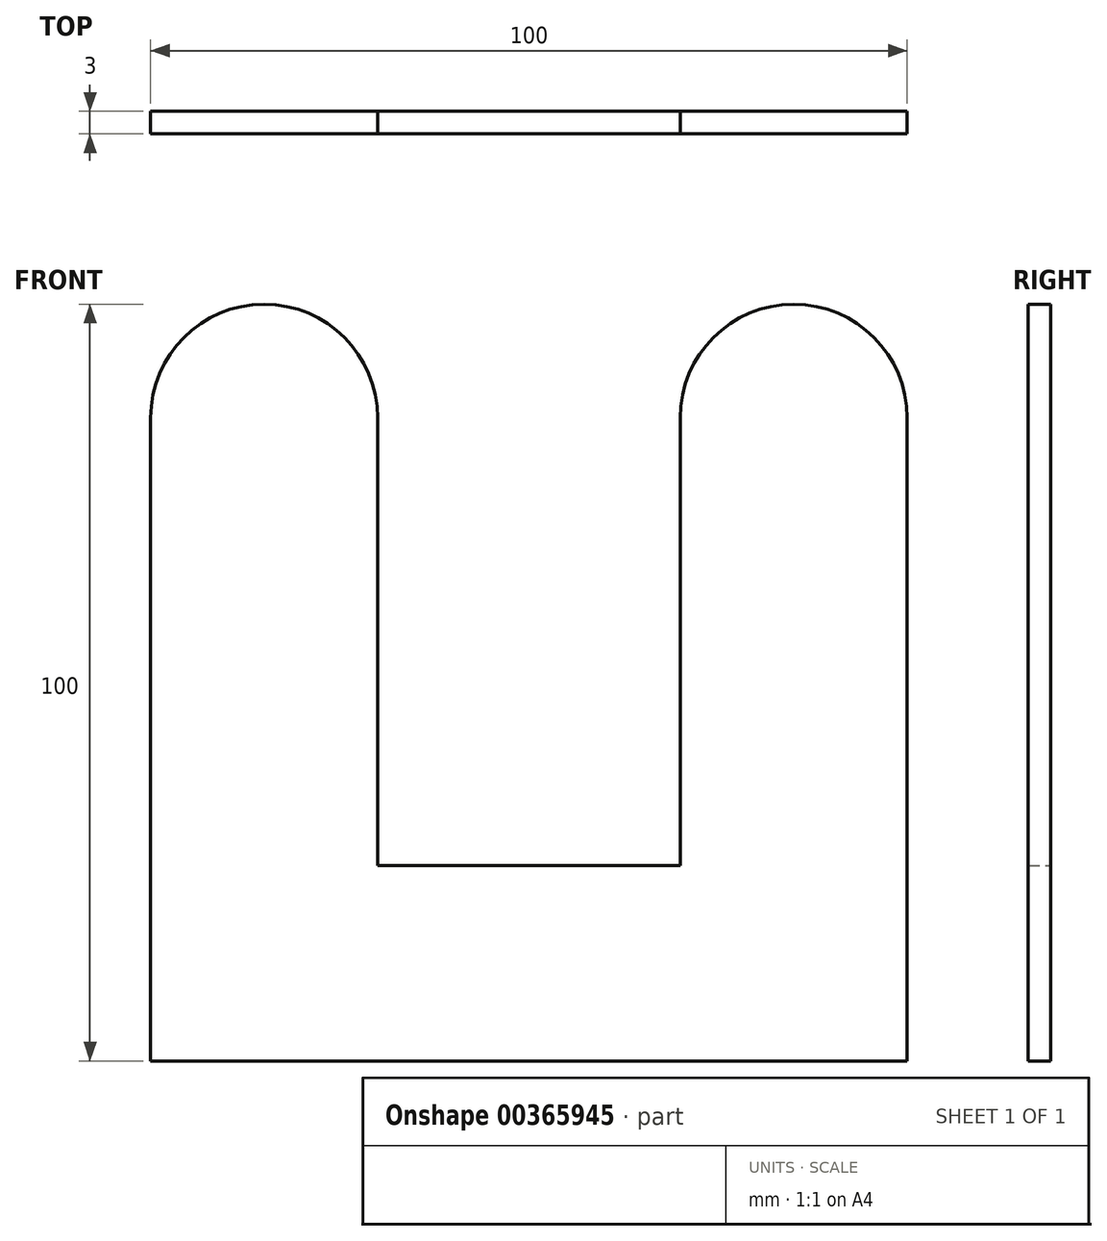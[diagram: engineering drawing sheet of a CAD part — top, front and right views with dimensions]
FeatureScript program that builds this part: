
annotation { "Feature Type Name" : "Feature", "Feature Type Description" : "" }
export const myFeature = defineFeature(function(context is Context, id is Id, definition is map)
    precondition{}
    {
        {
            var Q0;
            Q0=qCreatedBy(makeId("Front.planeOp"),FACE);
            var sketch = newSketch(context, id + "F0", { "sketchPlane" : qUnion([Q0])});
            skLineSegment(sketch, "E0.bottom", {"start": v(0, 0) * mm, "end": v(100, 0) * mm});
            skLineSegment(sketch, "E0.top", {"start": v(30, 25.83) * mm, "end": v(70, 25.83) * mm});
            skLineSegment(sketch, "E0.left", {"start": v(0, 0) * mm, "end": v(0, 25.83) * mm});
            skLineSegment(sketch, "E0.right", {"start": v(100, 0) * mm, "end": v(100, 25.83) * mm});
            skLineSegment(sketch, "E1.top", {"start": v(100, 100) * mm, "end": v(70, 100) * mm});
            skLineSegment(sketch, "E1.left", {"start": v(100, 25.83) * mm, "end": v(100, 100) * mm});
            skLineSegment(sketch, "E1.right", {"start": v(70, 25.83) * mm, "end": v(70, 100) * mm});
            skLineSegment(sketch, "E2.top", {"start": v(0, 100) * mm, "end": v(30, 100) * mm});
            skLineSegment(sketch, "E2.left", {"start": v(0, 25.83) * mm, "end": v(0, 100) * mm});
            skLineSegment(sketch, "E2.right", {"start": v(30, 25.83) * mm, "end": v(30, 100) * mm});
            skSolve(sketch);
        }
        {
            var Q0;
            Q0 = qSketchRegion(id + "F0", true);
            extrude(context, id + "F1", {"entities" : qUnion([Q0]), "depth" : 3 * mm});
        }
        {
            var Q0;
            Q0=makeQuery(id+"F1.opExtrude","SWEPT_EDGE",EDGE,{"disambiguationData":[OSD([sQuery(id+"F0.wireOp",EDGE,"E1.top"),sQuery(id+"F0.wireOp",EDGE,"E1.left")])]});
            var Q1;
            Q1=makeQuery(id+"F1.opExtrude","SWEPT_EDGE",EDGE,{"disambiguationData":[OSD([sQuery(id+"F0.wireOp",EDGE,"E1.top"),sQuery(id+"F0.wireOp",EDGE,"E1.right")])]});
            var Q2;
            Q2=makeQuery(id+"F1.opExtrude","SWEPT_EDGE",EDGE,{"disambiguationData":[OSD([sQuery(id+"F0.wireOp",EDGE,"E2.top"),sQuery(id+"F0.wireOp",EDGE,"E2.right")])]});
            var Q3;
            Q3=makeQuery(id+"F1.opExtrude","SWEPT_EDGE",EDGE,{"disambiguationData":[OSD([sQuery(id+"F0.wireOp",EDGE,"E2.top"),sQuery(id+"F0.wireOp",EDGE,"E2.left")])]});
            fillet(context, id + "F2", {"entities" : qUnion([Q0, Q1, Q2, Q3]), "radius" : 15 * mm, "tangentPropagation" : true, "allowEdgeOverflow" : false});
        }
    });
